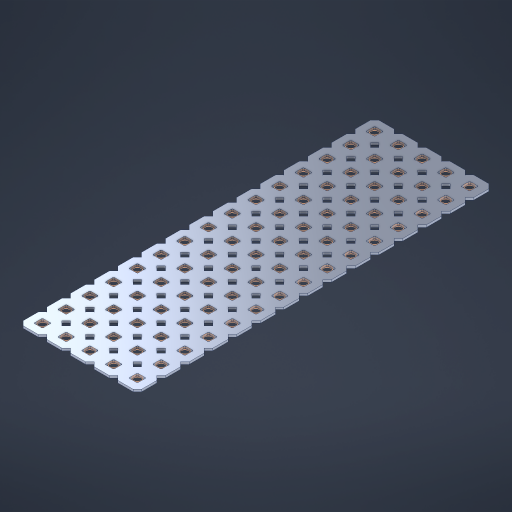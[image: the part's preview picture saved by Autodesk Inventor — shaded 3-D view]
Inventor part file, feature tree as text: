
AUTODESK INVENTOR PART (.ipt)
format: ipt  version: 2023 (Build 270158000, 158)  size: 1,132,544 bytes
history: native  units: in
note: dims shown in document units (in); Inventor stores cm internally (conversion verified against a paired STEP export)
features: other x76, extrude x74, sketch x2, pattern_linear x1
ambient origin geometry x8: Origin, YZ Plane, XZ Plane, XY Plane, X Axis, Y Axis, Z Axis, Center Point
bodies: Solid1 (feature_tree), Body (feature_tree)
feature tree (153):
  pattern_linear  "Rectangular Pattern1"  Spacing1=0.09in  [1 undecoded]
  sketch  "Sketch1"  dims[d1=0.5in]
  sketch  "Sketch2"  dims[d2=0.182in d3=0.09in d4=0.09in d5=0.09in d6=0.09in d7=0.09in d8=0.09in d9=0.09in d10=0.09in d11=0.02in d13=0.0in d14=0.172in d15=0.0625in d16=0.0in d19=0.5in d22=0.5in]
  other  "Srf1"
  other  "Srf126"
  other  "Srf127"
  other  "Srf128"
  other  "Srf129"
  other  "Srf130"
  other  "Srf131"
  other  "Srf250"
  other  "Srf251"
  other  "Srf252"
  other  "Srf253"
  other  "Srf254"
  other  "Srf255"
  other  "Srf256"
  other  "Srf257"
  other  "Srf268"
  other  "Srf269"
  other  "Srf270"
  other  "Srf271"
  other  "Srf272"
  other  "Srf273"
  other  "Srf274"
  other  "Srf275"
  other  "Srf276"
  other  "Srf277"
  other  "Srf278"
  other  "Srf279"
  other  "Srf280"
  other  "Srf281"
  other  "Srf282"
  other  "Srf293"
  other  "Srf294"
  other  "Srf295"
  other  "Srf296"
  other  "Srf297"
  other  "Srf298"
  other  "Srf299"
  other  "Srf300"
  other  "Srf301"
  other  "Srf302"
  other  "Srf303"
  other  "Srf304"
  other  "Srf305"
  other  "Srf306"
  other  "Srf307"
  other  "Srf318"
  other  "Srf319"
  other  "Srf320"
  other  "Srf321"
  other  "Srf322"
  other  "Srf323"
  other  "Srf324"
  other  "Srf325"
  other  "Srf326"
  other  "Srf327"
  other  "Srf328"
  other  "Srf329"
  other  "Srf330"
  other  "Srf331"
  other  "Srf332"
  other  "Srf343"
  other  "Srf344"
  other  "Srf345"
  other  "Srf346"
  other  "Srf347"
  other  "Srf348"
  other  "Srf349"
  other  "Srf350"
  other  "Srf351"
  other  "Srf352"
  other  "Srf353"
  other  "Srf354"
  other  "Srf355"
  other  "Srf356"
  other  "Srf357"
  other  "Circle"
  extrude  "ExtrusionSrf126"  Depth=0.09in
  extrude  "ExtrusionSrf127"  Depth=0.09in
  extrude  "ExtrusionSrf128"  Depth=0.09in
  extrude  "ExtrusionSrf129"  Depth=0.09in
  extrude  "ExtrusionSrf130"  Depth=0.09in
  extrude  "ExtrusionSrf131"  Depth=0.09in
  extrude  "ExtrusionSrf250"  Depth=0.09in
  extrude  "ExtrusionSrf251"  Depth=0.02in
  extrude  "ExtrusionSrf252"  TaperAngle=0.0deg  [1 undecoded]
  extrude  "ExtrusionSrf253"  Depth=0.5in
  extrude  "ExtrusionSrf254"  Depth=0.5in TaperAngle=0.0deg
  extrude  "ExtrusionSrf255"  Depth=0.5in
  extrude  "ExtrusionSrf256"  Depth=0.5in
  extrude  "ExtrusionSrf257"  [1 undecoded]
  extrude  "ExtrusionSrf268"  [1 undecoded]
  extrude  "ExtrusionSrf269"  [1 undecoded]
  extrude  "ExtrusionSrf270"  [1 undecoded]
  extrude  "ExtrusionSrf271"  [1 undecoded]
  extrude  "ExtrusionSrf272"  [1 undecoded]
  extrude  "ExtrusionSrf273"  [1 undecoded]
  extrude  "ExtrusionSrf274"  [1 undecoded]
  extrude  "ExtrusionSrf275"  [1 undecoded]
  extrude  "ExtrusionSrf276"  [1 undecoded]
  extrude  "ExtrusionSrf277"  [1 undecoded]
  extrude  "ExtrusionSrf278"  [1 undecoded]
  extrude  "ExtrusionSrf279"  [1 undecoded]
  extrude  "ExtrusionSrf280"  [1 undecoded]
  extrude  "ExtrusionSrf281"  [1 undecoded]
  extrude  "ExtrusionSrf282"  [1 undecoded]
  extrude  "ExtrusionSrf293"  [1 undecoded]
  extrude  "ExtrusionSrf294"  [1 undecoded]
  extrude  "ExtrusionSrf295"  [1 undecoded]
  extrude  "ExtrusionSrf296"  [1 undecoded]
  extrude  "ExtrusionSrf297"  [1 undecoded]
  extrude  "ExtrusionSrf298"  [1 undecoded]
  extrude  "ExtrusionSrf299"  [1 undecoded]
  extrude  "ExtrusionSrf300"  [1 undecoded]
  extrude  "ExtrusionSrf301"  [1 undecoded]
  extrude  "ExtrusionSrf302"  [1 undecoded]
  extrude  "ExtrusionSrf303"  [1 undecoded]
  extrude  "ExtrusionSrf304"  [1 undecoded]
  extrude  "ExtrusionSrf305"  [1 undecoded]
  extrude  "ExtrusionSrf306"  [1 undecoded]
  extrude  "ExtrusionSrf307"  [1 undecoded]
  extrude  "ExtrusionSrf318"  [1 undecoded]
  extrude  "ExtrusionSrf319"  [1 undecoded]
  extrude  "ExtrusionSrf320"  [1 undecoded]
  extrude  "ExtrusionSrf321"  [1 undecoded]
  extrude  "ExtrusionSrf322"  [1 undecoded]
  extrude  "ExtrusionSrf323"  [1 undecoded]
  extrude  "ExtrusionSrf324"  [1 undecoded]
  extrude  "ExtrusionSrf325"  [1 undecoded]
  extrude  "ExtrusionSrf326"  [1 undecoded]
  extrude  "ExtrusionSrf327"  [1 undecoded]
  extrude  "ExtrusionSrf328"  [1 undecoded]
  extrude  "ExtrusionSrf329"  [1 undecoded]
  extrude  "ExtrusionSrf330"  [1 undecoded]
  extrude  "ExtrusionSrf331"  [1 undecoded]
  extrude  "ExtrusionSrf332"  [1 undecoded]
  extrude  "ExtrusionSrf343"  [1 undecoded]
  extrude  "ExtrusionSrf344"  [1 undecoded]
  extrude  "ExtrusionSrf345"  [1 undecoded]
  extrude  "ExtrusionSrf346"  [1 undecoded]
  extrude  "ExtrusionSrf347"  [1 undecoded]
  extrude  "ExtrusionSrf348"  [1 undecoded]
  extrude  "ExtrusionSrf349"  [1 undecoded]
  extrude  "ExtrusionSrf350"  [1 undecoded]
  extrude  "ExtrusionSrf351"  [1 undecoded]
  extrude  "ExtrusionSrf352"  [1 undecoded]
  extrude  "ExtrusionSrf353"  [1 undecoded]
  extrude  "ExtrusionSrf354"  [1 undecoded]
  extrude  "ExtrusionSrf355"  [1 undecoded]
  extrude  "ExtrusionSrf356"  [1 undecoded]
  extrude  "ExtrusionSrf357"  [1 undecoded]
note: 63 required parameter values undecoded (feature->parameter linkage not recoverable at this tier; creation-order binding heuristic only, values carry confidence <= 0.55)
